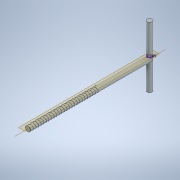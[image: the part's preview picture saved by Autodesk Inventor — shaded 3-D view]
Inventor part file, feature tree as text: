
AUTODESK INVENTOR PART (.ipt)
format: ipt  version: 2020 (Build 240168000, 168)  size: 619,008 bytes
history: native  units: in
note: dims shown in document units (in); Inventor stores cm internally (conversion verified against a paired STEP export)
features: sketch x3, extrude x2, other x2, helix x1, plane x1
ambient origin geometry x8: Origin, YZ Plane, XZ Plane, XY Plane, X Axis, Y Axis, Z Axis, Center Point
bodies: Solid1 (feature_tree)
feature tree (9):
  extrude  "Extrusion1"  Depth=47.2441in TaperAngle=0.0deg
  sketch  "Sketch2"  dims[d4=1.0in d5=1.0in d6=10.5996in d7=0.0in d8=90.0deg d9=90.0deg d10=0.0in d11=0.0in d12=0.9843in]
  other  "Work Axis1"
  helix  "Coil1"  [1 undecoded]
  plane  "Work Plane1"
  sketch  "Sketch3"  dims[d13=1.9685in d14=23.622in d15=0.0in]
  extrude  "Extrusion2"  Depth=0.9843in
  other  "Work Axis2"
  sketch  "Sketch1"  dims[d0=1.9685in d1=47.2441in d2=0.0in d3=0.1969in]
note: 1 required parameter value undecoded (feature->parameter linkage not recoverable at this tier; creation-order binding heuristic only, values carry confidence <= 0.55)
